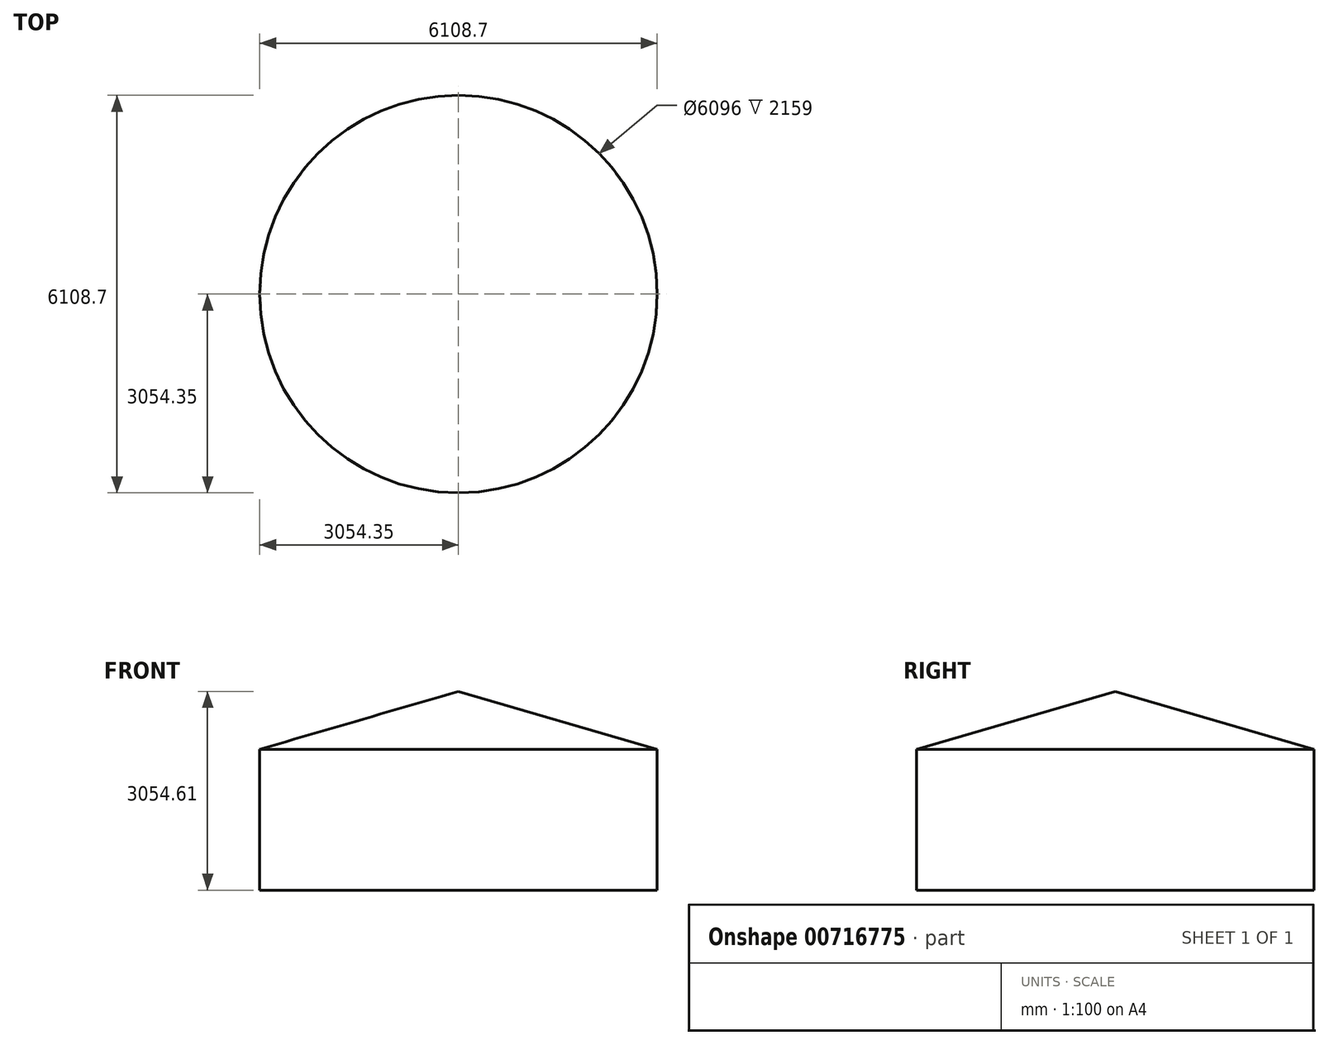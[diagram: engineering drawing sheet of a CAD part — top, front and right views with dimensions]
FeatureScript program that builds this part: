
annotation { "Feature Type Name" : "Feature", "Feature Type Description" : "" }
export const myFeature = defineFeature(function(context is Context, id is Id, definition is map)
    precondition{}
    {
        {
            var Q0;
            Q0=qCreatedBy(makeId("Front.planeOp"),FACE);
            var sketch = newSketch(context, id + "F0", { "sketchPlane" : qUnion([Q0])});
            skLineSegment(sketch, "E0", {"start": v(0, -2159) * mm, "end": v(3048, -2159) * mm, "construction": true});
            skLineSegment(sketch, "E1", {"start": v(3048, -2159) * mm, "end": v(3048, 0) * mm});
            skLineSegment(sketch, "E2", {"start": v(3048, 0) * mm, "end": v(0, 889) * mm});
            skLineSegment(sketch, "E3", {"start": v(0, 889) * mm, "end": v(0, -2159) * mm, "construction": true});
            skLineSegment(sketch, "E4.0", {"start": v(3054.35, 4.76) * mm, "end": v(0, 895.61) * mm});
            skLineSegment(sketch, "E4.1", {"start": v(3054.35, -2159) * mm, "end": v(3054.35, 4.76) * mm});
            skLineSegment(sketch, "E5", {"start": v(0, 895.61) * mm, "end": v(0, 889) * mm});
            skLineSegment(sketch, "E6", {"start": v(3048, -2159) * mm, "end": v(3054.35, -2159) * mm});
            skSolve(sketch);
        }
        {
            var Q0;
            Q0 = qSketchRegion(id + "F0", true);
            var Q1;
            Q1=sQuery(id+"F0.wireOp",EDGE,"E4.0");
            var Q2;
            Q2=sQuery(id+"F0.wireOp",EDGE,"E4.1");
            var Q3;
            Q3=sQuery(id+"F0.wireOp",EDGE,"E3");
            revolve(context, id + "F1", {"surfaceOperationType" : NewSurfaceOperationType.NEW, "entities" : qUnion([Q0]), "surfaceEntities" : qUnion([Q1, Q2]), "axis" : qUnion([Q3]), "revolveType" : RevolveType.FULL});
        }
    });
